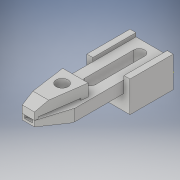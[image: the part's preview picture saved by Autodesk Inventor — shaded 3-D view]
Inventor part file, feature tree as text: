
AUTODESK INVENTOR PART (.ipt)
format: ipt  version: 2017 (Build 210142000, 142)  size: 243,200 bytes
history: native  units: in
note: dims shown in document units (in); Inventor stores cm internally (conversion verified against a paired STEP export)
features: sketch x7, extrude x6, plane x2, chamfer x2, split x2
ambient origin geometry x8: Origin, YZ Plane, XZ Plane, XY Plane, X Axis, Y Axis, Z Axis, Center Point
bodies: Solid1 (feature_tree), Solid2 (feature_tree), Solid3 (feature_tree), Solid4 (feature_tree), Solid5 (feature_tree)
feature tree (19):
  sketch  "Sketch1"  dims[d3=0.25in d10=0.136in]
  plane  "Work Plane2"
  extrude  "Extrusion3"  Depth=0.25in
  chamfer  "Chamfer2"  Distance=0.25in
  extrude  "Extrusion4"  Depth=0.5053in
  extrude  "Extrusion5"  Depth=0.25in
  split  "Split1"
  chamfer  "Chamfer3"  Distance=0.1982in
  extrude  "Extrusion6"  Depth=0.25in
  extrude  "Extrusion7"  Depth=0.25in
  sketch  "Sketch16"  dims[d52=0.2527in d53=0.5053in]
  plane  "Work Plane3"
  split  "Split2"
  extrude  "Extrusion8"  Depth=0.19in TaperAngle=0.0deg
  sketch  "Sketch12"  dims[d12=0.177in]
  sketch  "Sketch13"  dims[d13=0.2in]
  sketch  "Sketch14"  dims[d14=0.177in]
  sketch  "Sketch15"  dims[d15=1.0in d23=0.25in d24=0.5in]
  sketch  "Sketch17"  dims[d57=1.12in d58=1.12in d59=0.1982in d60=0.2527in d61=0.2527in d62=0.19in d63=0.0in d64=0.1in d65=0.45in d66=45.0deg d67=0.06in d68=0.7146in d69=0.7146in d70=0.145in d71=0.0346in d72=0.1982in d73=0.05in d74=0.0in d75=0.194in d76=0.198in d77=0.2in d78=0.0in d79=0.2in d80=0.08in d81=45.0deg d82=0.03in d83=0.0in d86=0.6734in d88=0.6734in d89=0.7in d90=0.7in d91=0.177in d92=0.35in d93=0.35in d94=0.25in d95=0.0in d96=0.25in d97=0.0in]
